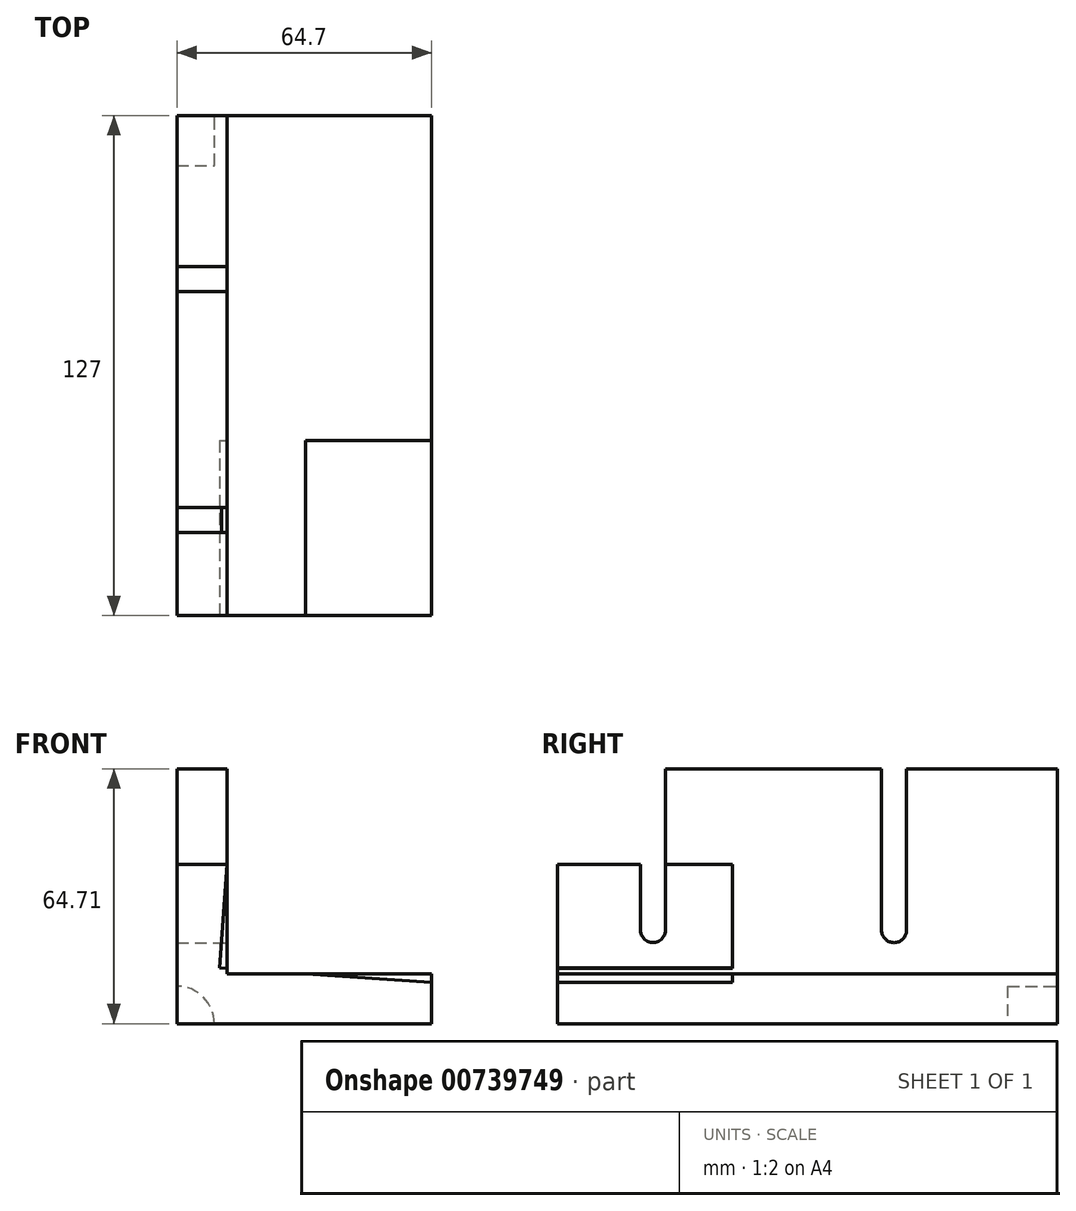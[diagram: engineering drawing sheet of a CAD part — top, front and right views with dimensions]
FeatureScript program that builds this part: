
annotation { "Feature Type Name" : "Feature", "Feature Type Description" : "" }
export const myFeature = defineFeature(function(context is Context, id is Id, definition is map)
    precondition{}
    {
        {
            var Q0;
            Q0=qCreatedBy(makeId("Front.planeOp"),FACE);
            var sketch = newSketch(context, id + "F0", { "sketchPlane" : qUnion([Q0])});
            skLineSegment(sketch, "E0", {"start": v(-33.64, 24.98) * mm, "end": v(-33.64, -39.73) * mm});
            skLineSegment(sketch, "E1", {"start": v(-33.64, -39.73) * mm, "end": v(31.06, -39.73) * mm});
            skLineSegment(sketch, "E2", {"start": v(31.06, -39.73) * mm, "end": v(31.06, 24.98) * mm});
            skLineSegment(sketch, "E3", {"start": v(-33.64, 24.98) * mm, "end": v(31.06, 24.98) * mm});
            skSolve(sketch);
        }
        {
            var Q0;
            Q0=makeQuery(id+"F0.imprint","IMPRINT",FACE,{"disambiguationData":[TD([[makeQuery(id+"F0.imprint","IMPRINT",EDGE,{"derivedFrom":sQuery(id+"F0.wireOp",EDGE,"E0")}),1.0]])]});
            extrude(context, id + "F1", {"entities" : qUnion([Q0]), "oppositeDirection" : true, "depth" : 127 * mm, "offsetDistance" : 25.4 * mm});
        }
        {
            var Q0;
            Q0=makeQuery(id+"F1.opExtrude","CAP_FACE",FACE,{"disambiguationData":[OSD([sQuery(id+"F0.wireOp",EDGE,"E0"),sQuery(id+"F0.wireOp",EDGE,"E1"),sQuery(id+"F0.wireOp",EDGE,"E2"),sQuery(id+"F0.wireOp",EDGE,"E3")])],"isStart":false});
            var sketch = newSketch(context, id + "F2", { "sketchPlane" : qUnion([Q0])});
            skLineSegment(sketch, "E4", {"start": v(33.64, -39.73) * mm, "end": v(33.64, -27.03) * mm});
            skLineSegment(sketch, "E5", {"start": v(33.64, -27.03) * mm, "end": v(20.94, -27.03) * mm});
            skLineSegment(sketch, "E6", {"start": v(20.94, -27.03) * mm, "end": v(20.94, -39.73) * mm});
            skLineSegment(sketch, "E7", {"start": v(20.94, -27.03) * mm, "end": v(-31.06, -27.03) * mm});
            skLineSegment(sketch, "E8", {"start": v(20.94, -27.03) * mm, "end": v(20.94, 24.98) * mm});
            skSolve(sketch);
        }
        {
            var Q0;
            {var subQ0=sQuery(id+"F2.wireOp",EDGE,"E7");Q0=makeQuery(id+"F2.imprint","IMPRINT",FACE,{"disambiguationData":[TD([[makeQuery(id+"F2.imprint","IMPRINT",EDGE,{"derivedFrom":subQ0}),-1.0]])]});}
            extrude(context, id + "F3", {"entities" : qUnion([Q0]), "operationType" : NewBodyOperationType.REMOVE, "endBound" : BoundingType.THROUGH_ALL, "oppositeDirection" : true, "depth" : 55.76 * mm, "offsetDistance" : 25.4 * mm});
        }
        {
            var Q0;
            Q0=makeQuery(id+"F1.opExtrude","CAP_FACE",FACE,{"disambiguationData":[OSD([sQuery(id+"F0.wireOp",EDGE,"E0"),sQuery(id+"F0.wireOp",EDGE,"E1"),sQuery(id+"F0.wireOp",EDGE,"E2"),sQuery(id+"F0.wireOp",EDGE,"E3")])],"isStart":true});
            var sketch = newSketch(context, id + "F4", { "sketchPlane" : qUnion([Q0])});
            skLineSegment(sketch, "E9", {"start": v(-20.94, 24.98) * mm, "end": v(-19.25, 24.98) * mm});
            skLineSegment(sketch, "E10", {"start": v(-22.78, -25.5) * mm, "end": v(-19.25, 24.98) * mm});
            skLineSegment(sketch, "E11", {"start": v(-22.78, -25.5) * mm, "end": v(31.06, -29.27) * mm});
            skLineSegment(sketch, "E12", {"start": v(-20.94, 24.98) * mm, "end": v(-33.64, 24.98) * mm});
            skLineSegment(sketch, "E13", {"start": v(-33.64, 24.98) * mm, "end": v(-33.64, -39.73) * mm});
            skLineSegment(sketch, "E14", {"start": v(-33.64, -39.73) * mm, "end": v(31.06, -39.73) * mm});
            skLineSegment(sketch, "E15", {"start": v(31.06, -39.73) * mm, "end": v(31.06, -29.27) * mm});
            skSolve(sketch);
        }
        {
            var Q0;
            {var subQ0=sQuery(id+"F4.wireOp",EDGE,"E11");var subQ1=sQuery(id+"F0.wireOp",EDGE,"E2");var subQ2=makeQuery(id+"F1.opExtrude","CAP_EDGE",EDGE,{"disambiguationData":[OSD([subQ1])],"isStart":true});var subQ3=makeQuery(id+"F4.imprint","INTERSECT",VERTEX,{"derivedFrom":[subQ2,subQ0,sQuery(id+"F4.wireOp",EDGE,"E15")]});Q0=makeQuery(id+"F4.imprint","IMPRINT",FACE,{"disambiguationData":[TD([[makeQuery(id+"F4.imprint","IMPRINT",EDGE,{"disambiguationData":[TD([[subQ3,1.0]])],"derivedFrom":subQ0}),1.0]])]});}
            var Q1;
            {var subQ0=sQuery(id+"F4.wireOp",EDGE,"E11");var subQ1=sQuery(id+"F4.wireOp",EDGE,"E10");var subQ2=makeQuery(id+"F4.imprint","INTERSECT",VERTEX,{"derivedFrom":[subQ1,subQ0]});Q1=makeQuery(id+"F4.imprint","IMPRINT",FACE,{"disambiguationData":[TD([[makeQuery(id+"F4.imprint","IMPRINT",EDGE,{"disambiguationData":[TD([[subQ2,-1.0]])],"derivedFrom":subQ1}),-1.0]])]});}
            extrude(context, id + "F5", {"entities" : qUnion([Q0, Q1]), "operationType" : NewBodyOperationType.REMOVE, "oppositeDirection" : true, "depth" : 44.45 * mm, "offsetDistance" : 25.4 * mm});
        }
        {
            var Q0;
            Q0=makeQuery(id+"F3.boolean.opBoolean","COPY",FACE,{"derivedFrom":makeQuery(id+"F3.opExtrude","SWEPT_FACE",FACE,{"disambiguationData":[OSD([sQuery(id+"F2.wireOp",EDGE,"E8")])]})});
            var sketch = newSketch(context, id + "F6", { "sketchPlane" : qUnion([Q0])});
            skLineSegment(sketch, "E16", {"start": v(27.44, 24.98) * mm, "end": v(127, 24.98) * mm});
            skLineSegment(sketch, "E17", {"start": v(127, 24.98) * mm, "end": v(127, -27.03) * mm});
            skLineSegment(sketch, "E18", {"start": v(127, -27.03) * mm, "end": v(0, -27.03) * mm});
            skLineSegment(sketch, "E19", {"start": v(0, -27.03) * mm, "end": v(0, 24.98) * mm});
            skLineSegment(sketch, "E20", {"start": v(0, 24.98) * mm, "end": v(21.09, 24.98) * mm});
            skArc(sketch, "E21", {"start": v(82.35, -15.98) * mm, "mid": v(85.53, -19.15) * mm, "end": v(88.7, -15.98) * mm});
            skLineSegment(sketch, "E22", {"start": v(88.7, -15.98) * mm, "end": v(88.7, 24.98) * mm});
            skLineSegment(sketch, "E23", {"start": v(82.35, -15.98) * mm, "end": v(82.35, 24.98) * mm});
            skArc(sketch, "E24", {"start": v(21.09, -15.98) * mm, "mid": v(24.26, -19.15) * mm, "end": v(27.44, -15.98) * mm});
            skLineSegment(sketch, "E25", {"start": v(21.09, -15.98) * mm, "end": v(21.09, 24.98) * mm});
            skLineSegment(sketch, "E26", {"start": v(27.44, -15.98) * mm, "end": v(27.44, 24.98) * mm});
            skLineSegment(sketch, "E27", {"start": v(27.44, 24.98) * mm, "end": v(21.09, 24.98) * mm});
            skSolve(sketch);
        }
        {
            var Q0;
            {var subQ1=sQuery(id+"F6.wireOp",EDGE,"c31WWHYK-vBc0-QJFG-3EGz-c6wR2XxRCZ5n");var subQ4=sQuery(id+"F6.wireOp",EDGE,"BnuWwshu-QowS-UM11-6egq-2gLvmHulIOIC");var subQ5=makeQuery(id+"F6.imprint","INTERSECT",VERTEX,{"derivedFrom":[subQ1,subQ4]});Q0=makeQuery(id+"F6.imprint","IMPRINT",FACE,{"disambiguationData":[TD([[makeQuery(id+"F6.imprint","IMPRINT",EDGE,{"disambiguationData":[TD([[subQ5,-1.0]])],"derivedFrom":subQ1}),1.0]])]});}
            var Q1;
            {var subQ0=sQuery(id+"F6.wireOp",EDGE,"PxgFI6bS-cj6o-HxTh-fpXl-rELYx5VuJGPC");var subQ9=sQuery(id+"F6.wireOp",EDGE,"BnuWwshu-QowS-UM11-6egq-2gLvmHulIOIC");var subQ10=makeQuery(id+"F6.imprint","INTERSECT",VERTEX,{"derivedFrom":[subQ0,subQ9]});Q1=makeQuery(id+"F6.imprint","IMPRINT",FACE,{"disambiguationData":[TD([[makeQuery(id+"F6.imprint","IMPRINT",EDGE,{"disambiguationData":[TD([[subQ10,-1.0]])],"derivedFrom":subQ0}),-1.0]])]});}
            var Q2;
            Q2=makeQuery(id+"F6.imprint","IMPRINT",FACE,{"disambiguationData":[TD([[makeQuery(id+"F6.imprint","IMPRINT",EDGE,{"derivedFrom":sQuery(id+"F6.wireOp",EDGE,"nVCfulUX-UBZk-rReu-1cFz-JZFjZ0D3dsWO")}),1.0]])]});
            var Q3;
            {var subQ0=sQuery(id+"F6.wireOp",EDGE,"BnuWwshu-QowS-UM11-6egq-2gLvmHulIOIC");var subQ1=sQuery(id+"F2.wireOp",EDGE,"E8");var subQ2=sQuery(id+"F0.wireOp",EDGE,"E3");var subQ3=makeQuery(id+"F3.boolean.opBoolean","COPY",EDGE,{"derivedFrom":makeQuery(id+"F3.opExtrude","SWEPT_EDGE",EDGE,{"disambiguationData":[OSD([subQ2,subQ1])]})});var subQ4=makeQuery(id+"F6.imprint","INTERSECT",VERTEX,{"derivedFrom":[subQ3,subQ0]});Q3=makeQuery(id+"F6.imprint","IMPRINT",FACE,{"disambiguationData":[TD([[makeQuery(id+"F6.imprint","IMPRINT",EDGE,{"disambiguationData":[TD([[subQ4,-1.0]])],"derivedFrom":subQ3}),-1.0]])]});}
            var Q4;
            {var subQ0=sQuery(id+"F6.wireOp",EDGE,"E20");var subQ1=sQuery(id+"F6.wireOp",EDGE,"GWAlOemz-n7tp-SVu9-tSwS-dO0S4uVOhK2H");var subQ2=makeQuery(id+"F6.imprint","INTERSECT",VERTEX,{"derivedFrom":[subQ1,subQ0]});Q4=makeQuery(id+"F6.imprint","IMPRINT",FACE,{"disambiguationData":[TD([[makeQuery(id+"F6.imprint","IMPRINT",EDGE,{"disambiguationData":[TD([[subQ2,-1.0]])],"derivedFrom":subQ0}),-1.0]])]});}
            var Q5;
            {var subQ0=sQuery(id+"F6.wireOp",EDGE,"YNUtTdzb-W802-iu6F-8lba-iVoMnU8XWFkd");Q5=makeQuery(id+"F6.imprint","IMPRINT",FACE,{"disambiguationData":[TD([[makeQuery(id+"F6.imprint","IMPRINT",EDGE,{"derivedFrom":subQ0}),1.0]])]});}
            var Q6;
            Q6=makeQuery(id+"F6.imprint","IMPRINT",FACE,{"disambiguationData":[TD([[makeQuery(id+"F6.imprint","IMPRINT",EDGE,{"derivedFrom":sQuery(id+"F6.wireOp",EDGE,"f8IW44Pr-O293-7rfo-ai8i-kcAhvm2oJwU2")}),1.0]])]});
            var Q7;
            {var subQ0=sQuery(id+"F6.wireOp",EDGE,"E27");Q7=makeQuery(id+"F6.imprint","IMPRINT",FACE,{"disambiguationData":[TD([[makeQuery(id+"F6.imprint","IMPRINT",EDGE,{"derivedFrom":subQ0}),-1.0]])]});}
            var Q8;
            {var subQ0=sQuery(id+"F6.wireOp",EDGE,"E24");Q8=makeQuery(id+"F6.imprint","IMPRINT",FACE,{"disambiguationData":[TD([[makeQuery(id+"F6.imprint","IMPRINT",EDGE,{"derivedFrom":subQ0}),1.0]])]});}
            var Q9;
            Q9=makeQuery(id+"F6.imprint","IMPRINT",FACE,{"disambiguationData":[TD([[makeQuery(id+"F6.imprint","IMPRINT",EDGE,{"derivedFrom":sQuery(id+"F6.wireOp",EDGE,"E21")}),1.0]])]});
            extrude(context, id + "F7", {"entities" : qUnion([Q0, Q1, Q2, Q3, Q4, Q5, Q6, Q7, Q8, Q9]), "operationType" : NewBodyOperationType.REMOVE, "endBound" : BoundingType.THROUGH_ALL, "oppositeDirection" : true, "depth" : 25.4 * mm, "offsetDistance" : 25.4 * mm});
        }
        {
            var Q0;
            Q0=makeQuery(id+"F1.opExtrude","CAP_FACE",FACE,{"disambiguationData":[OSD([sQuery(id+"F0.wireOp",EDGE,"E0"),sQuery(id+"F0.wireOp",EDGE,"E1"),sQuery(id+"F0.wireOp",EDGE,"E2"),sQuery(id+"F0.wireOp",EDGE,"E3")])],"isStart":false});
            var sketch = newSketch(context, id + "F8", { "sketchPlane" : qUnion([Q0])});
            skCircle(sketch, "E28", {"center": v(33.64, -39.73) * mm, "radius": 9.53 * mm});
            skSolve(sketch);
        }
        {
            var Q0;
            {var subQ0=sQuery(id+"F8.wireOp",EDGE,"E28");var subQ1=makeQuery(id+"F1.opExtrude","CAP_EDGE",EDGE,{"disambiguationData":[OSD([sQuery(id+"F0.wireOp",EDGE,"E0")])],"isStart":false});var subQ2=makeQuery(id+"F8.imprint","INTERSECT",VERTEX,{"derivedFrom":[subQ1,subQ0]});Q0=makeQuery(id+"F8.imprint","IMPRINT",FACE,{"disambiguationData":[TD([[makeQuery(id+"F8.imprint","IMPRINT",EDGE,{"disambiguationData":[TD([[subQ2,-1.0]])],"derivedFrom":subQ0}),1.0]])]});}
            extrude(context, id + "F9", {"entities" : qUnion([Q0]), "operationType" : NewBodyOperationType.REMOVE, "oppositeDirection" : true, "depth" : 12.7 * mm, "offsetDistance" : 25.4 * mm});
        }
    });
